# Revit family: G-Fire_Coupling_Grv_Fig.577_Imperial
name_source: partatom
category: Pipe Fittings
revit_build: Autodesk Revit 2018 (Build: 20170630_0700(x64)
units: mm (PartAtom-declared; Revit-internal decimal feet)

## family parameters
Always vertical = Yes
Cut with Voids When Loaded = No
OmniClass Number = 23.60.30.11.14
OmniClass Title = Pipework Fittings
Part Type = Flange
Round Connector Dimension = Use Radius
Shared = Yes
Work Plane-Based = No

## types (3) — shared parameters
BoltType = Yes
COBie = Yes
COBie.Type = Yes
COBie.Type.AssetType = Fixed
COBie.Type.Category = Pr_65_52_63_11:Fittings
COBie.Type.DurationUnit = year
COBie.Type.Manufacturer = Tyco Fire Protection Products
COBie.Type.Material = Ductile Iron
COBie.Type.ModelReference = Grv Coupling (Gpf)
COBie.Type.NominalHeight = 0' - 0"
COBie.Type.NominalLength = 0' - 0"
COBie.Type.NominalWidth = 0' - 0"
COBie.Type.WarrantyDurationUnit = year
COBie.Type.WarrantyGuarantorParts = http://tycofsbp.com
Description = Grooved Rigid Coupling
Lookup Table Name = Coupling-Tyco-577
Loss Method = Not Defined
Manufacturer = Tyco
Meterial = Ductile iron ASTM A536
Model = Fig.577
Product Name = G-FIRE Figure 577
G-FIRE Figure 577
Grooved Rigid Coupling
Technical Data Sheet No = TFP1854
URL = www.tyco-fire.com
zero-valued in all types: COBie.Type.ReplacementCost

## per-type parameters (varying)
| type | Coating | Finish |
| G-Fire_Coupling_Grv_Fig.577_Red3000 | Tyco - Red RAL3000 | Tyco - Red RAL3000 |
| G-Fire_Coupling_Grv_Fig.577_Galvanized | Tyco - Galvanized | Tyco - Galvanized |
| G-Fire_Coupling_Grv_Fig.577_Orange | Tyco - Orange Paint | Tyco - Orange Paint |

## geometry (parser evidence)
native form markers: Sweep x9
no freeform markers — native parametric forms only
